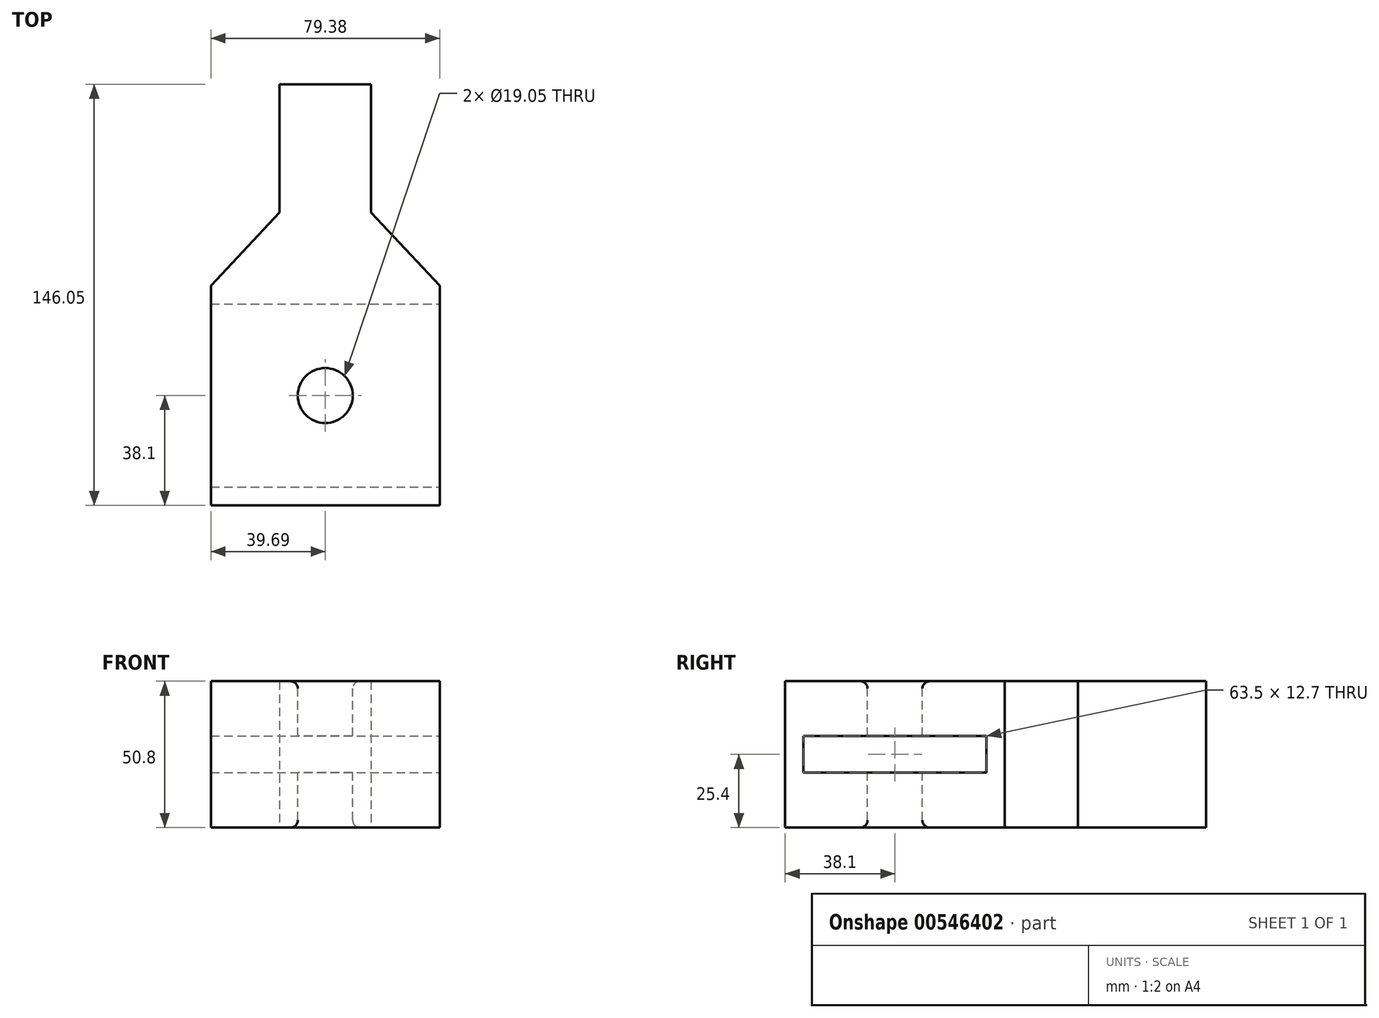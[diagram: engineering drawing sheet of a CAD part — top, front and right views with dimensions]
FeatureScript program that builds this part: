
annotation { "Feature Type Name" : "Feature", "Feature Type Description" : "" }
export const myFeature = defineFeature(function(context is Context, id is Id, definition is map)
    precondition{}
    {
        {
            var Q0;
            Q0=qCreatedBy(makeId("Top.planeOp"),FACE);
            var sketch = newSketch(context, id + "F0", { "sketchPlane" : qUnion([Q0])});
            skLineSegment(sketch, "E0", {"start": v(-39.69, -38.1) * mm, "end": v(39.69, -38.1) * mm});
            skLineSegment(sketch, "E1", {"start": v(39.69, -38.1) * mm, "end": v(39.69, 38.1) * mm});
            skLineSegment(sketch, "E2", {"start": v(39.69, 38.1) * mm, "end": v(15.87, 63.5) * mm});
            skLineSegment(sketch, "E3", {"start": v(15.87, 63.5) * mm, "end": v(15.87, 107.95) * mm});
            skLineSegment(sketch, "E4", {"start": v(15.88, 107.95) * mm, "end": v(-15.88, 107.95) * mm});
            skLineSegment(sketch, "E5", {"start": v(-15.88, 107.95) * mm, "end": v(-15.88, 63.5) * mm});
            skLineSegment(sketch, "E6", {"start": v(-15.87, 63.5) * mm, "end": v(-39.69, 38.1) * mm});
            skLineSegment(sketch, "E7", {"start": v(-39.69, 38.1) * mm, "end": v(-39.69, -38.1) * mm});
            skLineSegment(sketch, "E8", {"start": v(0, 107.95) * mm, "end": v(0, -38.1) * mm, "construction": true});
            skLineSegment(sketch, "E9", {"start": v(39.69, 0) * mm, "end": v(-39.69, 0) * mm, "construction": true});
            skLineSegment(sketch, "E10", {"start": v(98.48, 107.95) * mm, "end": v(98.48, -38.1) * mm, "construction": true});
            skPoint(sketch, "E11", {"position": v(98.48, 34.92) * mm});
            skSolve(sketch);
        }
        {
            var Q0;
            Q0=makeQuery(id+"F0.imprint","IMPRINT",FACE,{"disambiguationData":[TD([[makeQuery(id+"F0.imprint","IMPRINT",EDGE,{"derivedFrom":sQuery(id+"F0.wireOp",EDGE,"E0")}),1.0]])]});
            extrude(context, id + "F1", {"entities" : qUnion([Q0]), "depth" : 50.8 * mm, "offsetDistance" : 25.4 * mm});
        }
        {
            var Q0;
            Q0=makeQuery(id+"F1.opExtrude","CAP_FACE",FACE,{"disambiguationData":[OSD([sQuery(id+"F0.wireOp",EDGE,"E0"),sQuery(id+"F0.wireOp",EDGE,"E1"),sQuery(id+"F0.wireOp",EDGE,"E2"),sQuery(id+"F0.wireOp",EDGE,"E3"),sQuery(id+"F0.wireOp",EDGE,"E4"),sQuery(id+"F0.wireOp",EDGE,"E5"),sQuery(id+"F0.wireOp",EDGE,"E6"),sQuery(id+"F0.wireOp",EDGE,"E7")])],"isStart":false});
            var sketch = newSketch(context, id + "F2", { "sketchPlane" : qUnion([Q0])});
            skCircle(sketch, "E12", {"center": v(0, 0) * mm, "radius": 9.53 * mm});
            skSolve(sketch);
        }
        {
            var Q0;
            Q0=makeQuery(id+"F2.imprint","IMPRINT",FACE,{"disambiguationData":[TD([[makeQuery(id+"F2.imprint","IMPRINT",EDGE,{"derivedFrom":sQuery(id+"F2.wireOp",EDGE,"E12")}),1.0]])]});
            extrude(context, id + "F3", {"entities" : qUnion([Q0]), "operationType" : NewBodyOperationType.REMOVE, "endBound" : BoundingType.THROUGH_ALL, "oppositeDirection" : true, "depth" : 25.4 * mm, "offsetDistance" : 25.4 * mm});
        }
        {
            var Q0;
            Q0=makeQuery(id+"F3.boolean.opBoolean","INTERSECT",EDGE,{"derivedFrom":[makeQuery(id+"F1.opExtrude","CAP_FACE",FACE,{"disambiguationData":[OSD([sQuery(id+"F0.wireOp",EDGE,"E0"),sQuery(id+"F0.wireOp",EDGE,"E1"),sQuery(id+"F0.wireOp",EDGE,"E2"),sQuery(id+"F0.wireOp",EDGE,"E3"),sQuery(id+"F0.wireOp",EDGE,"E4"),sQuery(id+"F0.wireOp",EDGE,"E5"),sQuery(id+"F0.wireOp",EDGE,"E6"),sQuery(id+"F0.wireOp",EDGE,"E7")])],"isStart":true}),makeQuery(id+"F3.opExtrude","SWEPT_FACE",FACE,{"disambiguationData":[OSD([sQuery(id+"F2.wireOp",EDGE,"E12")])]})]});
            var Q1;
            Q1=makeQuery(id+"F3.boolean.opBoolean","COPY",FACE,{"derivedFrom":makeQuery(id+"F3.opExtrude","SWEPT_FACE",FACE,{"disambiguationData":[OSD([sQuery(id+"F2.wireOp",EDGE,"E12")])]})});
            fillet(context, id + "F4", {"entities" : qUnion([Q0, Q1]), "radius" : 2.54 * mm, "tangentPropagation" : true, "allowEdgeOverflow" : false});
        }
        {
            var Q0;
            Q0=qCreatedBy(makeId("Right.planeOp"),FACE);
            var sketch = newSketch(context, id + "F5", { "sketchPlane" : qUnion([Q0])});
            skLineSegment(sketch, "E13.bottom", {"start": v(31.75, 31.75) * mm, "end": v(-31.75, 31.75) * mm});
            skLineSegment(sketch, "E13.top", {"start": v(31.75, 19.05) * mm, "end": v(-31.75, 19.05) * mm});
            skLineSegment(sketch, "E13.left", {"start": v(31.75, 31.75) * mm, "end": v(31.75, 19.05) * mm});
            skLineSegment(sketch, "E13.right", {"start": v(-31.75, 31.75) * mm, "end": v(-31.75, 19.05) * mm});
            skPoint(sketch, "E13.middle", {"position": v(0, 25.4) * mm});
            skSolve(sketch);
        }
        {
            var Q0;
            Q0 = qSketchRegion(id + "F5", true);
            extrude(context, id + "F6", {"entities" : qUnion([Q0]), "operationType" : NewBodyOperationType.REMOVE, "endBound" : BoundingType.THROUGH_ALL, "oppositeDirection" : true, "depth" : 12.7 * mm, "offsetDistance" : 25.4 * mm, "hasSecondDirection" : true, "secondDirectionBound" : SecondDirectionBoundingType.THROUGH_ALL, "secondDirectionOppositeDirection" : false, "secondDirectionDepth" : 12.7 * mm});
        }
    });
